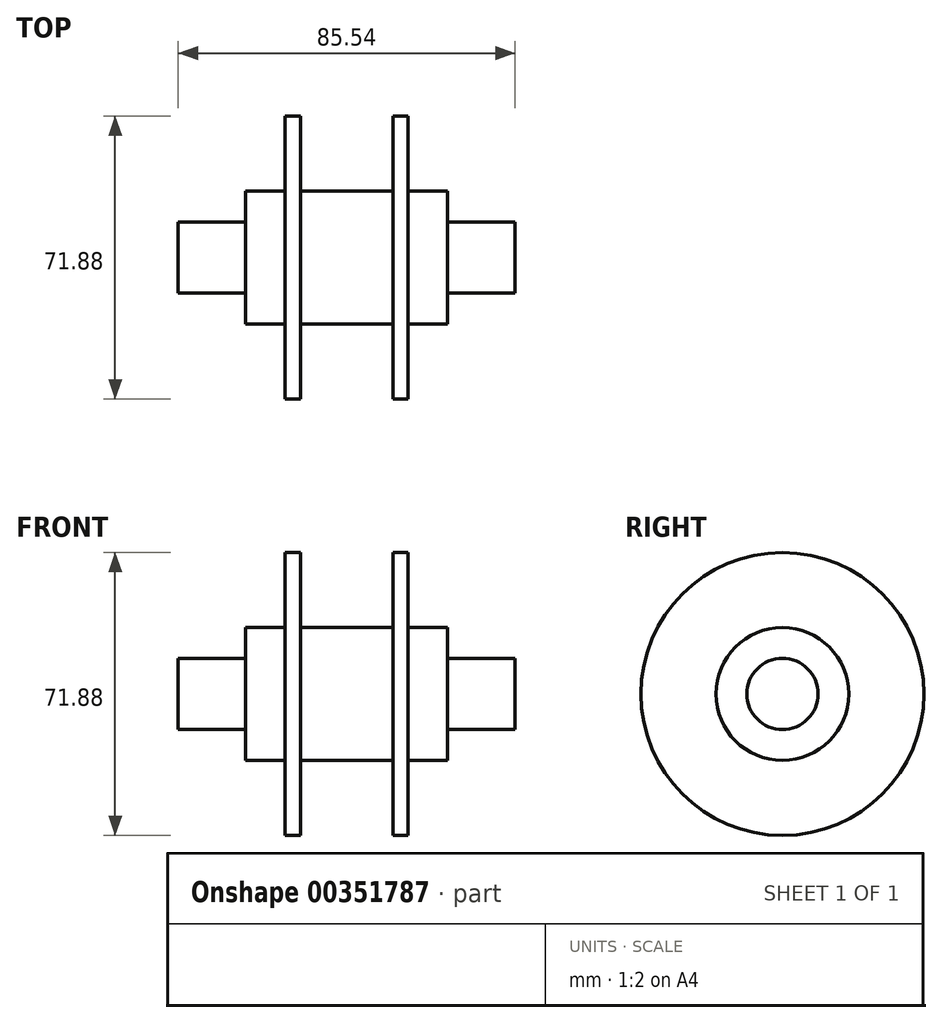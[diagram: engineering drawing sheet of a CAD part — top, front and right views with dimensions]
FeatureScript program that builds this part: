
annotation { "Feature Type Name" : "Feature", "Feature Type Description" : "" }
export const myFeature = defineFeature(function(context is Context, id is Id, definition is map)
    precondition{}
    {
        {
            var Q0;
            Q0=qCreatedBy(makeId("Front.planeOp"),FACE);
            var sketch = newSketch(context, id + "F0", { "sketchPlane" : qUnion([Q0])});
            skLineSegment(sketch, "E0", {"start": v(0, 0) * mm, "end": v(-42.77, 0) * mm});
            skLineSegment(sketch, "E1", {"start": v(-42.77, 0) * mm, "end": v(-42.77, 9.04) * mm});
            skLineSegment(sketch, "E2", {"start": v(-42.77, 9.04) * mm, "end": v(-25.63, 9.04) * mm});
            skLineSegment(sketch, "E3", {"start": v(-25.63, 9.04) * mm, "end": v(-25.63, 16.87) * mm});
            skLineSegment(sketch, "E4", {"start": v(-25.63, 16.87) * mm, "end": v(-15.65, 16.87) * mm});
            skLineSegment(sketch, "E5", {"start": v(-15.65, 16.87) * mm, "end": v(-15.65, 35.94) * mm});
            skLineSegment(sketch, "E6", {"start": v(-15.65, 35.94) * mm, "end": v(-11.73, 35.94) * mm});
            skLineSegment(sketch, "E7", {"start": v(-11.73, 35.94) * mm, "end": v(-11.73, 16.87) * mm});
            skLineSegment(sketch, "E8", {"start": v(-11.73, 16.87) * mm, "end": v(0, 16.87) * mm});
            skLineSegment(sketch, "E9", {"start": v(0, 16.87) * mm, "end": v(0, 0) * mm});
            skLineSegment(sketch, "E10.MirrorCS", {"start": v(11.73, 16.87) * mm, "end": v(0, 16.87) * mm});
            skLineSegment(sketch, "E11.MirrorCS", {"start": v(11.73, 35.94) * mm, "end": v(11.73, 16.87) * mm});
            skLineSegment(sketch, "E12.MirrorCS", {"start": v(15.65, 16.87) * mm, "end": v(15.65, 35.94) * mm});
            skLineSegment(sketch, "E13.MirrorCS", {"start": v(25.63, 9.04) * mm, "end": v(25.63, 16.87) * mm});
            skLineSegment(sketch, "E14.MirrorCS", {"start": v(25.63, 16.87) * mm, "end": v(15.65, 16.87) * mm});
            skLineSegment(sketch, "E15.MirrorCS", {"start": v(42.77, 0) * mm, "end": v(42.77, 9.04) * mm});
            skLineSegment(sketch, "E16.MirrorCS", {"start": v(0, 0) * mm, "end": v(42.77, 0) * mm});
            skLineSegment(sketch, "E17.MirrorCS", {"start": v(42.77, 9.04) * mm, "end": v(25.63, 9.04) * mm});
            skLineSegment(sketch, "E18.MirrorCS", {"start": v(15.65, 35.94) * mm, "end": v(11.73, 35.94) * mm});
            skSolve(sketch);
        }
        {
            var Q0;
            Q0 = qSketchRegion(id + "F0", true);
            var Q1;
            Q1=sQuery(id+"F0.wireOp",EDGE,"E0");
            revolve(context, id + "F1", {"entities" : qUnion([Q0]), "axis" : qUnion([Q1]), "revolveType" : RevolveType.FULL});
        }
    });
